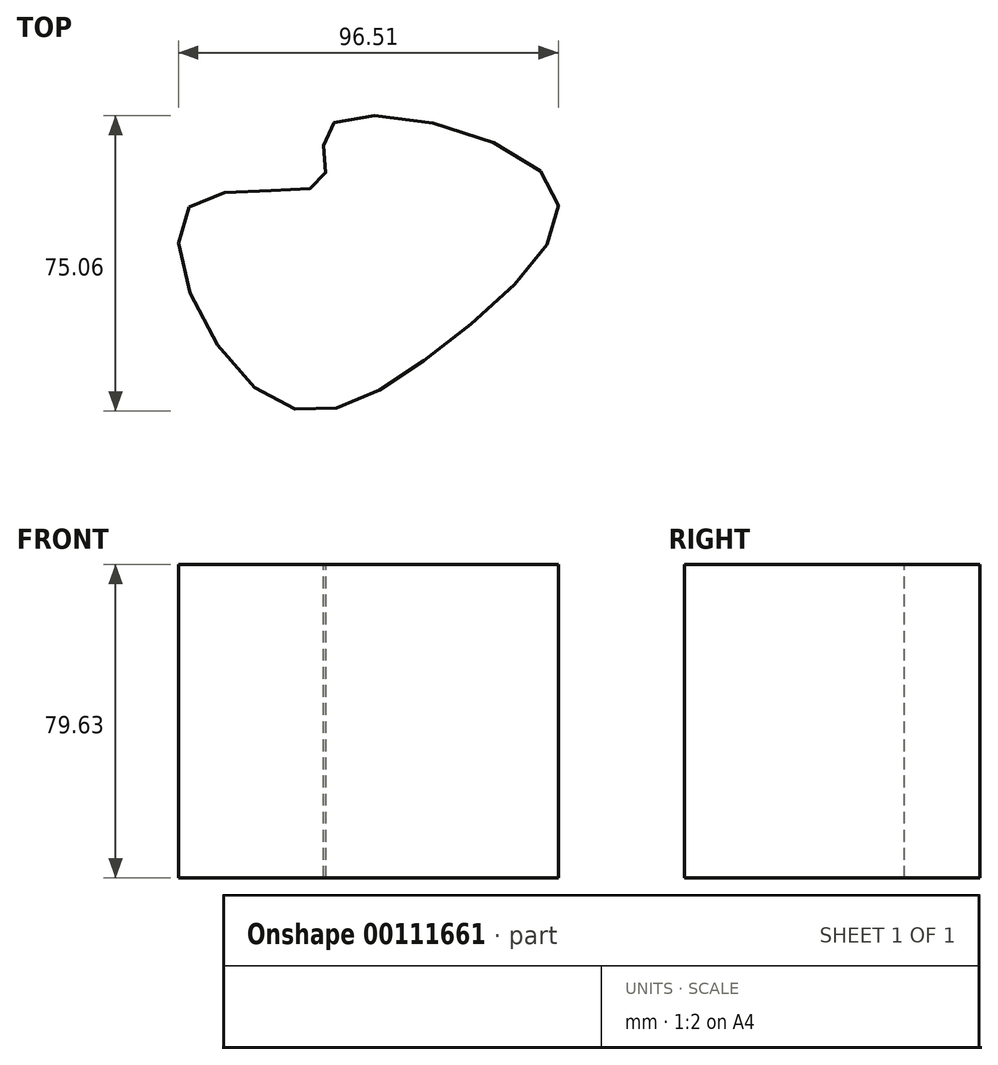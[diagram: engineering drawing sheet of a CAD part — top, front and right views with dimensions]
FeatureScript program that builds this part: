
annotation { "Feature Type Name" : "Feature", "Feature Type Description" : "" }
export const myFeature = defineFeature(function(context is Context, id is Id, definition is map)
    precondition{}
    {
        {
            var Q0;
            Q0=qCreatedBy(makeId("Top.planeOp"),FACE);
            var sketch = newSketch(context, id + "F0", { "sketchPlane" : qUnion([Q0])});
            skFitSpline(sketch, "E0", {"points": [v(-45.52, 31.18) * mm, v(-11.82, 37.38) * mm, v(-9.88, 51.71) * mm, v(46.28, 37.38) * mm, v(19.27, -3.92) * mm, v(-25.38, -17.24) * mm, v(-45.52, 31.18) * mm]});
            skSolve(sketch);
        }
        {
            var Q0;
            Q0=makeQuery(id+"F0.imprint","IMPRINT",FACE,{"disambiguationData":[TD([[makeQuery(id+"F0.imprint","IMPRINT",EDGE,{"derivedFrom":sQuery(id+"F0.wireOp",EDGE,"E0")}),-1.0]])]});
            extrude(context, id + "F1", {"entities" : qUnion([Q0]), "depth" : 25.4 * mm});
        }
        {
            var Q0;
            Q0 = qSketchRegion(id + "F0", true);
            extrude(context, id + "F2", {"entities" : qUnion([Q0]), "operationType" : NewBodyOperationType.ADD, "depth" : 79.63 * mm});
        }
    });
